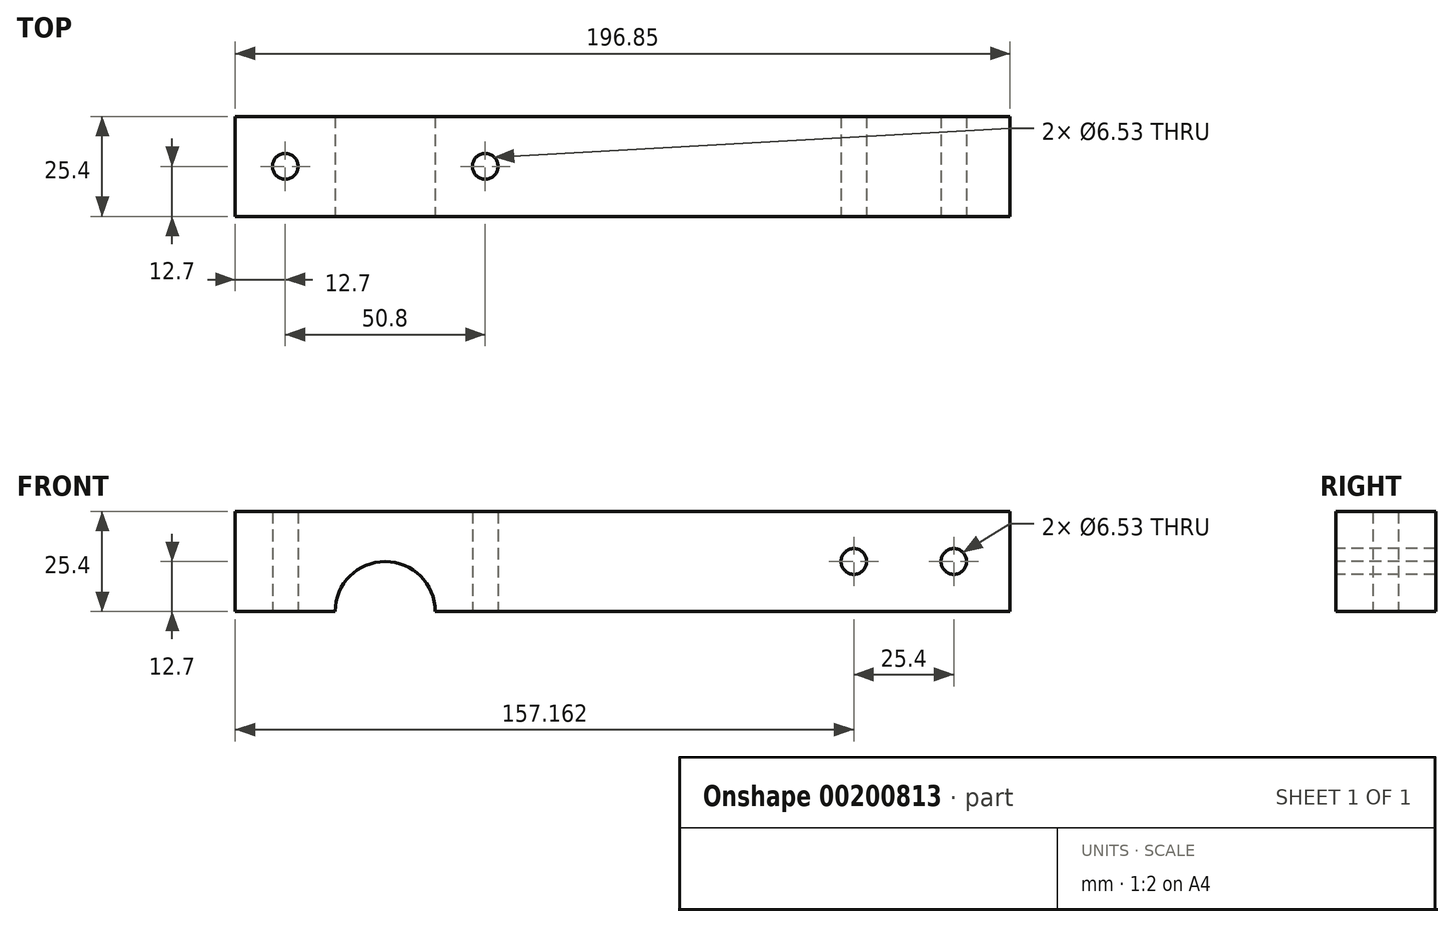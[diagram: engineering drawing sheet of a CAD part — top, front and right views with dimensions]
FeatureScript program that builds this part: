
annotation { "Feature Type Name" : "Feature", "Feature Type Description" : "" }
export const myFeature = defineFeature(function(context is Context, id is Id, definition is map)
    precondition{}
    {
        {
            var Q0;
            Q0=qCreatedBy(makeId("Front.planeOp"),FACE);
            var sketch = newSketch(context, id + "F0", { "sketchPlane" : qUnion([Q0])});
            skLineSegment(sketch, "E0.bottom", {"start": v(0, 0) * mm, "end": v(196.85, 0) * mm});
            skLineSegment(sketch, "E0.top", {"start": v(0, 25.4) * mm, "end": v(196.85, 25.4) * mm});
            skLineSegment(sketch, "E0.left", {"start": v(0, 0) * mm, "end": v(0, 25.4) * mm});
            skLineSegment(sketch, "E0.right", {"start": v(196.85, 0) * mm, "end": v(196.85, 25.4) * mm});
            skSolve(sketch);
        }
        {
            var Q0;
            Q0=makeQuery(id+"F0.imprint","IMPRINT",FACE,{"disambiguationData":[TD([[makeQuery(id+"F0.imprint","IMPRINT",EDGE,{"derivedFrom":sQuery(id+"F0.wireOp",EDGE,"E0.bottom")}),1.0]])]});
            extrude(context, id + "F1", {"entities" : qUnion([Q0]), "depth" : 25.4 * mm});
        }
        {
            var Q0;
            Q0=makeQuery(id+"F1.opExtrude","CAP_FACE",FACE,{"disambiguationData":[OSD([sQuery(id+"F0.wireOp",EDGE,"E0.bottom"),sQuery(id+"F0.wireOp",EDGE,"E0.top"),sQuery(id+"F0.wireOp",EDGE,"E0.left"),sQuery(id+"F0.wireOp",EDGE,"E0.right")])],"isStart":false});
            var sketch = newSketch(context, id + "F2", { "sketchPlane" : qUnion([Q0])});
            skCircle(sketch, "E1", {"center": v(38.1, 0) * mm, "radius": 12.7 * mm});
            skSolve(sketch);
        }
        {
            var Q0;
            Q0=makeQuery(id+"F1.opExtrude","CAP_FACE",FACE,{"disambiguationData":[OSD([sQuery(id+"F0.wireOp",EDGE,"E0.bottom"),sQuery(id+"F0.wireOp",EDGE,"E0.top"),sQuery(id+"F0.wireOp",EDGE,"E0.left"),sQuery(id+"F0.wireOp",EDGE,"E0.right")])],"isStart":false});
            var sketch = newSketch(context, id + "F3", { "sketchPlane" : qUnion([Q0])});
            skPoint(sketch, "E2", {"position": v(157.16, 12.7) * mm});
            skPoint(sketch, "E3", {"position": v(182.56, 12.7) * mm});
            skSolve(sketch);
        }
        {
            var Q0;
            Q0 = qSketchRegion(id + "F2", true);
            extrude(context, id + "F4", {"entities" : qUnion([Q0]), "operationType" : NewBodyOperationType.REMOVE, "oppositeDirection" : true, "depth" : 25.4 * mm});
        }
        {
            var Q0;
            Q0=sQuery(id+"F3.wireOp",VERTEX,"E2");
            var Q1;
            Q1=sQuery(id+"F3.wireOp",VERTEX,"E3");
            var Q2;
            Q2=makeQuery(id+"F1.opExtrude","SWEPT_BODY",BODY,{"disambiguationData":[OSD([sQuery(id+"F0.wireOp",EDGE,"E0.bottom"),sQuery(id+"F0.wireOp",EDGE,"E0.top"),sQuery(id+"F0.wireOp",EDGE,"E0.left"),sQuery(id+"F0.wireOp",EDGE,"E0.right")])]});
            hole(context, id + "F5", {"style" : HoleStyle.SIMPLE, "endStyle" : HoleEndStyle.THROUGH, "standardTappedOrClearance" : lookupTablePath({ "standard" : "ANSI", "engagement" : "75%", "pitch" : "18 tpi", "size" : "5/16", "type" : "Tapped" }), "standardBlindInLast" : lookupTablePath({ "standard" : "ANSI", "engagement" : "75%", "pitch" : "18 tpi", "size" : "5/16", "type" : "Tapped" }), "holeDiameter" : 6.53 * mm, "locations" : qUnion([Q0, Q1]), "scope" : qUnion([Q2]), "isTappedThrough" : true, "majorDiameter" : 7.94 * mm, "showTappedDepth" : true});
        }
        {
            var Q0;
            {var subQ1=sQuery(id+"F0.wireOp",EDGE,"E0.left");var subQ3=sQuery(id+"F0.wireOp",EDGE,"E0.bottom");Q0=makeQuery(id+"F4.boolean.opBoolean","SPLIT",FACE,{"disambiguationData":[TD([makeQuery(id+"F1.opExtrude","SWEPT_FACE",FACE,{"disambiguationData":[OSD([subQ1])]})])],"derivedFrom":makeQuery(id+"F1.opExtrude","SWEPT_FACE",FACE,{"disambiguationData":[OSD([subQ3])]})});}
            var sketch = newSketch(context, id + "F6", { "sketchPlane" : qUnion([Q0])});
            skPoint(sketch, "E4", {"position": v(12.7, 12.7) * mm});
            skPoint(sketch, "E5", {"position": v(63.5, 12.7) * mm});
            skSolve(sketch);
        }
        {
            var Q0;
            Q0=sQuery(id+"F6.wireOp",VERTEX,"E4");
            var Q1;
            Q1=sQuery(id+"F6.wireOp",VERTEX,"E5");
            var Q2;
            Q2=makeQuery(id+"F1.opExtrude","SWEPT_BODY",BODY,{"disambiguationData":[OSD([sQuery(id+"F0.wireOp",EDGE,"E0.bottom"),sQuery(id+"F0.wireOp",EDGE,"E0.top"),sQuery(id+"F0.wireOp",EDGE,"E0.left"),sQuery(id+"F0.wireOp",EDGE,"E0.right")])]});
            hole(context, id + "F7", {"style" : HoleStyle.SIMPLE, "endStyle" : HoleEndStyle.THROUGH, "standardTappedOrClearance" : lookupTablePath({ "standard" : "ANSI", "engagement" : "75%", "pitch" : "18 tpi", "size" : "5/16", "type" : "Tapped" }), "standardBlindInLast" : lookupTablePath({ "standard" : "ANSI", "engagement" : "75%", "pitch" : "18 tpi", "size" : "5/16", "type" : "Tapped" }), "holeDiameter" : 6.53 * mm, "locations" : qUnion([Q0, Q1]), "scope" : qUnion([Q2]), "isTappedThrough" : true, "majorDiameter" : 7.94 * mm, "showTappedDepth" : true});
        }
    });
